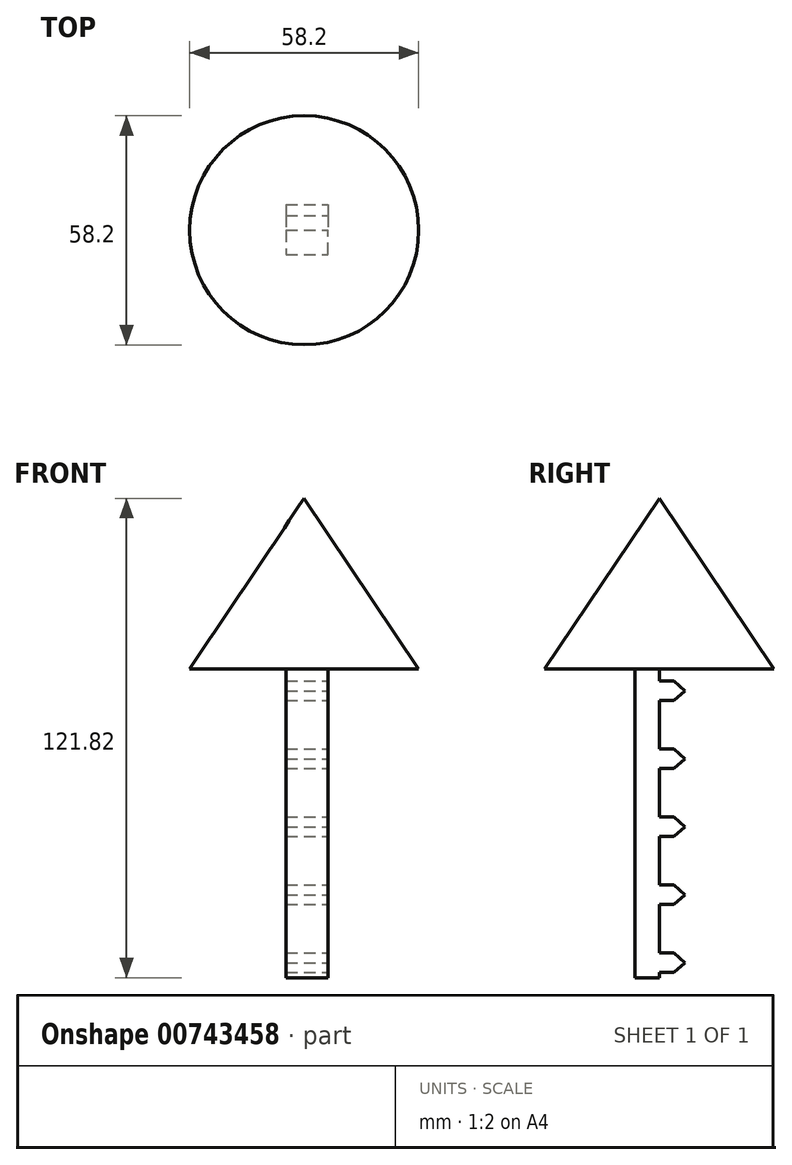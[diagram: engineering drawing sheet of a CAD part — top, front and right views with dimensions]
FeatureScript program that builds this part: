
annotation { "Feature Type Name" : "Feature", "Feature Type Description" : "" }
export const myFeature = defineFeature(function(context is Context, id is Id, definition is map)
    precondition{}
    {
        {
            var Q0;
            Q0=qCreatedBy(makeId("Right.planeOp"),FACE);
            var sketch = newSketch(context, id + "F0", { "sketchPlane" : qUnion([Q0])});
            skLineSegment(sketch, "E0", {"start": v(-29.1, 0) * mm, "end": v(0, 43.33) * mm});
            skLineSegment(sketch, "E1", {"start": v(0, 43.33) * mm, "end": v(0, 0) * mm});
            skLineSegment(sketch, "E2", {"start": v(0, 0) * mm, "end": v(-29.1, 0) * mm});
            skLineSegment(sketch, "E3", {"start": v(61.1, 0) * mm, "end": v(61.1, 40.81) * mm});
            skLineSegment(sketch, "E4.MirrorCS", {"start": v(151.3, 0) * mm, "end": v(122.2, 43.33) * mm});
            skLineSegment(sketch, "E5.MirrorCS", {"start": v(122.2, 43.33) * mm, "end": v(122.2, 0) * mm});
            skLineSegment(sketch, "E6.MirrorCS", {"start": v(122.2, 0) * mm, "end": v(151.3, 0) * mm});
            skSolve(sketch);
        }
        {
            var Q0;
            Q0=makeQuery(id+"F0.imprint","IMPRINT",FACE,{"disambiguationData":[TD([[makeQuery(id+"F0.imprint","IMPRINT",EDGE,{"derivedFrom":sQuery(id+"F0.wireOp",EDGE,"E0")}),-1.0]])]});
            var Q1;
            Q1=sQuery(id+"F0.wireOp",EDGE,"E1");
            revolve(context, id + "F1", {"surfaceOperationType" : NewSurfaceOperationType.NEW, "entities" : qUnion([Q0]), "axis" : qUnion([Q1]), "revolveType" : RevolveType.FULL});
        }
        {
            var Q0;
            Q0=makeQuery(id+"F0.imprint","IMPRINT",FACE,{"disambiguationData":[TD([[makeQuery(id+"F0.imprint","IMPRINT",EDGE,{"derivedFrom":sQuery(id+"F0.wireOp",EDGE,"E4.MirrorCS")}),1.0]])]});
            var Q1;
            Q1=sQuery(id+"F0.wireOp",EDGE,"E5.MirrorCS");
            revolve(context, id + "F2", {"surfaceOperationType" : NewSurfaceOperationType.NEW, "entities" : qUnion([Q0]), "axis" : qUnion([Q1]), "revolveType" : RevolveType.FULL});
        }
        {
            var Q0;
            Q0=makeQuery(id+"F1.opRevolve","SWEPT_FACE",FACE,{"disambiguationData":[OSD([sQuery(id+"F0.wireOp",EDGE,"E2")])]});
            var sketch = newSketch(context, id + "F3", { "sketchPlane" : qUnion([Q0])});
            skLineSegment(sketch, "E7.bottom", {"start": v(-6.7, 6.14) * mm, "end": v(6, 6.14) * mm});
            skLineSegment(sketch, "E7.top", {"start": v(-6.7, -6.56) * mm, "end": v(6, -6.56) * mm});
            skLineSegment(sketch, "E7.left", {"start": v(-6.7, 6.14) * mm, "end": v(-6.7, -6.56) * mm});
            skLineSegment(sketch, "E7.right", {"start": v(6, 6.14) * mm, "end": v(6, -6.56) * mm});
            skSolve(sketch);
        }
        {
            var Q0;
            Q0=makeQuery(id+"F3.imprint","IMPRINT",FACE,{"disambiguationData":[TD([[makeQuery(id+"F3.imprint","IMPRINT",EDGE,{"derivedFrom":sQuery(id+"F3.wireOp",EDGE,"E7.bottom")}),-1.0]])]});
            extrude(context, id + "F4", {"entities" : qUnion([Q0]), "operationType" : NewBodyOperationType.ADD, "depth" : 78.49 * mm, "offsetDistance" : 25.4 * mm});
        }
        {
            var Q0;
            Q0=makeQuery(id+"F4.opExtrude","SWEPT_FACE",FACE,{"disambiguationData":[OSD([sQuery(id+"F3.wireOp",EDGE,"E7.right")])]});
            var sketch = newSketch(context, id + "F5", { "sketchPlane" : qUnion([Q0])});
            skLineSegment(sketch, "E8.0.2.0", {"start": v(0, 52.43) * mm, "end": v(6.56, 52.43) * mm});
            skLineSegment(sketch, "E8.0.2.1", {"start": v(0, 47.52) * mm, "end": v(0, 52.43) * mm});
            skLineSegment(sketch, "E8.0.2.2", {"start": v(6.56, 47.52) * mm, "end": v(0, 47.52) * mm});
            skLineSegment(sketch, "E8.0.3.0", {"start": v(0, 112.37) * mm, "end": v(6.56, 112.37) * mm});
            skLineSegment(sketch, "E8.0.3.1", {"start": v(0, 107.47) * mm, "end": v(0, 112.37) * mm});
            skLineSegment(sketch, "E8.0.3.2", {"start": v(6.56, 107.47) * mm, "end": v(0, 107.47) * mm});
            skLineSegment(sketch, "E8.0.4.0", {"start": v(0, 172.31) * mm, "end": v(6.56, 172.31) * mm});
            skLineSegment(sketch, "E8.0.4.1", {"start": v(0, 167.41) * mm, "end": v(0, 172.31) * mm});
            skLineSegment(sketch, "E8.0.4.2", {"start": v(6.56, 167.41) * mm, "end": v(0, 167.41) * mm});
            skLineSegment(sketch, "E9", {"start": v(0, -3.1) * mm, "end": v(3.77, -3.1) * mm});
            skLineSegment(sketch, "E10", {"start": v(3.77, -3.1) * mm, "end": v(6.56, -5.61) * mm});
            skLineSegment(sketch, "E11", {"start": v(6.56, -5.61) * mm, "end": v(3.77, -7.97) * mm});
            skLineSegment(sketch, "E12", {"start": v(3.77, -7.97) * mm, "end": v(0, -7.97) * mm});
            skLineSegment(sketch, "E13", {"start": v(0, -7.97) * mm, "end": v(0, -3.1) * mm});
            skLineSegment(sketch, "E14.0.1.0", {"start": v(0, -20.38) * mm, "end": v(3.77, -20.38) * mm});
            skLineSegment(sketch, "E14.0.1.1", {"start": v(3.77, -25.24) * mm, "end": v(0, -25.24) * mm});
            skLineSegment(sketch, "E14.0.1.2", {"start": v(0, -25.24) * mm, "end": v(0, -20.38) * mm});
            skLineSegment(sketch, "E14.0.1.3", {"start": v(6.56, -22.88) * mm, "end": v(3.77, -25.24) * mm});
            skLineSegment(sketch, "E14.0.1.4", {"start": v(3.77, -20.38) * mm, "end": v(6.56, -22.88) * mm});
            skLineSegment(sketch, "E14.0.2.0", {"start": v(0, -37.65) * mm, "end": v(3.77, -37.65) * mm});
            skLineSegment(sketch, "E14.0.2.1", {"start": v(3.77, -42.51) * mm, "end": v(0, -42.51) * mm});
            skLineSegment(sketch, "E14.0.2.2", {"start": v(0, -42.51) * mm, "end": v(0, -37.65) * mm});
            skLineSegment(sketch, "E14.0.2.3", {"start": v(6.56, -40.16) * mm, "end": v(3.77, -42.51) * mm});
            skLineSegment(sketch, "E14.0.2.4", {"start": v(3.77, -37.65) * mm, "end": v(6.56, -40.16) * mm});
            skLineSegment(sketch, "E14.0.3.0", {"start": v(0, -54.93) * mm, "end": v(3.77, -54.93) * mm});
            skLineSegment(sketch, "E14.0.3.1", {"start": v(3.77, -59.78) * mm, "end": v(0, -59.78) * mm});
            skLineSegment(sketch, "E14.0.3.2", {"start": v(0, -59.78) * mm, "end": v(0, -54.93) * mm});
            skLineSegment(sketch, "E14.0.3.3", {"start": v(6.56, -57.43) * mm, "end": v(3.77, -59.78) * mm});
            skLineSegment(sketch, "E14.0.3.4", {"start": v(3.77, -54.93) * mm, "end": v(6.56, -57.43) * mm});
            skLineSegment(sketch, "E14.0.4.0", {"start": v(0, -72.2) * mm, "end": v(3.77, -72.2) * mm});
            skLineSegment(sketch, "E14.0.4.1", {"start": v(3.77, -77.05) * mm, "end": v(0, -77.05) * mm});
            skLineSegment(sketch, "E14.0.4.2", {"start": v(0, -77.05) * mm, "end": v(0, -72.2) * mm});
            skLineSegment(sketch, "E14.0.4.3", {"start": v(6.56, -74.7) * mm, "end": v(3.77, -77.05) * mm});
            skLineSegment(sketch, "E14.0.4.4", {"start": v(3.77, -72.2) * mm, "end": v(6.56, -74.7) * mm});
            skLineSegment(sketch, "E14.direction1", {"start": v(0, -7.97) * mm, "end": v(25.4, -7.97) * mm, "construction": true});
            skLineSegment(sketch, "E14.direction2", {"start": v(0, -7.97) * mm, "end": v(0, -25.24) * mm, "construction": true});
            skPoint(sketch, "E15.oppositeSnap0", {"position": v(0, -71.83) * mm});
            skLineSegment(sketch, "E15.bottom", {"start": v(-6.14, 0) * mm, "end": v(0, 0) * mm});
            skLineSegment(sketch, "E15.top", {"start": v(-6.14, -78.49) * mm, "end": v(0, -78.49) * mm});
            skLineSegment(sketch, "E15.left", {"start": v(-6.14, 0) * mm, "end": v(-6.14, -78.49) * mm});
            skLineSegment(sketch, "E15.right", {"start": v(0, 0) * mm, "end": v(0, -78.49) * mm});
            skSolve(sketch);
        }
        {
            var Q0;
            {var subQ15=sQuery(id+"F5.wireOp",EDGE,"E15.bottom");Q0=makeQuery(id+"F5.imprint","IMPRINT",FACE,{"disambiguationData":[TD([[makeQuery(id+"F5.imprint","IMPRINT",EDGE,{"derivedFrom":subQ15}),-1.0]])]});}
            var Q1;
            {var subQ1=sQuery(id+"F5.wireOp",EDGE,"E9");Q1=makeQuery(id+"F5.imprint","IMPRINT",FACE,{"disambiguationData":[TD([[makeQuery(id+"F5.imprint","IMPRINT",EDGE,{"derivedFrom":subQ1}),-1.0]])]});}
            var Q2;
            {var subQ1=sQuery(id+"F5.wireOp",EDGE,"E14.0.1.0");Q2=makeQuery(id+"F5.imprint","IMPRINT",FACE,{"disambiguationData":[TD([[makeQuery(id+"F5.imprint","IMPRINT",EDGE,{"derivedFrom":subQ1}),-1.0]])]});}
            var Q3;
            {var subQ1=sQuery(id+"F5.wireOp",EDGE,"E14.0.2.0");Q3=makeQuery(id+"F5.imprint","IMPRINT",FACE,{"disambiguationData":[TD([[makeQuery(id+"F5.imprint","IMPRINT",EDGE,{"derivedFrom":subQ1}),-1.0]])]});}
            var Q4;
            {var subQ1=sQuery(id+"F5.wireOp",EDGE,"E14.0.3.0");Q4=makeQuery(id+"F5.imprint","IMPRINT",FACE,{"disambiguationData":[TD([[makeQuery(id+"F5.imprint","IMPRINT",EDGE,{"derivedFrom":subQ1}),-1.0]])]});}
            var Q5;
            {var subQ1=sQuery(id+"F5.wireOp",EDGE,"E14.0.4.0");Q5=makeQuery(id+"F5.imprint","IMPRINT",FACE,{"disambiguationData":[TD([[makeQuery(id+"F5.imprint","IMPRINT",EDGE,{"derivedFrom":subQ1}),-1.0]])]});}
            var Q6;
            {var subQ2=sQuery(id+"F5.wireOp",EDGE,"E14.0.5.0");Q6=makeQuery(id+"F5.imprint","IMPRINT",FACE,{"disambiguationData":[TD([[makeQuery(id+"F5.imprint","IMPRINT",EDGE,{"derivedFrom":subQ2}),-1.0]])]});}
            var Q7;
            {var subQ1=sQuery(id+"F5.wireOp",EDGE,"E14.0.6.0");Q7=makeQuery(id+"F5.imprint","IMPRINT",FACE,{"disambiguationData":[TD([[makeQuery(id+"F5.imprint","IMPRINT",EDGE,{"derivedFrom":subQ1}),-1.0]])]});}
            var Q8;
            {var subQ1=sQuery(id+"F5.wireOp",EDGE,"E14.0.7.0");Q8=makeQuery(id+"F5.imprint","IMPRINT",FACE,{"disambiguationData":[TD([[makeQuery(id+"F5.imprint","IMPRINT",EDGE,{"derivedFrom":subQ1}),-1.0]])]});}
            var Q9;
            {var subQ1=sQuery(id+"F5.wireOp",EDGE,"E14.0.8.0");Q9=makeQuery(id+"F5.imprint","IMPRINT",FACE,{"disambiguationData":[TD([[makeQuery(id+"F5.imprint","IMPRINT",EDGE,{"derivedFrom":subQ1}),-1.0]])]});}
            var Q10;
            {var subQ1=sQuery(id+"F5.wireOp",EDGE,"E14.0.9.0");Q10=makeQuery(id+"F5.imprint","IMPRINT",FACE,{"disambiguationData":[TD([[makeQuery(id+"F5.imprint","IMPRINT",EDGE,{"derivedFrom":subQ1}),-1.0]])]});}
            extrude(context, id + "F6", {"entities" : qUnion([Q0, Q1, Q2, Q3, Q4, Q5, Q6, Q7, Q8, Q9, Q10]), "operationType" : NewBodyOperationType.ADD, "oppositeDirection" : true, "depth" : 56.13 * mm, "offsetDistance" : 25.4 * mm});
        }
        {
            var Q0;
            Q0=makeQuery(id+"F2.opRevolve","SWEPT_BODY",BODY,{"disambiguationData":[OSD([sQuery(id+"F0.wireOp",EDGE,"E4.MirrorCS"),sQuery(id+"F0.wireOp",EDGE,"E5.MirrorCS"),sQuery(id+"F0.wireOp",EDGE,"E6.MirrorCS")])]});
            deleteBodies(context, id + "F7", {"entities" : qUnion([Q0])});
        }
        {
            var Q0;
            {var subQ1=sQuery(id+"F5.wireOp",EDGE,"E9");Q0=makeQuery(id+"F5.imprint","IMPRINT",FACE,{"disambiguationData":[TD([[makeQuery(id+"F5.imprint","IMPRINT",EDGE,{"derivedFrom":subQ1}),1.0]])]});}
            var Q1;
            {var subQ3=sQuery(id+"F5.wireOp",EDGE,"E11");Q1=makeQuery(id+"F5.imprint","IMPRINT",FACE,{"disambiguationData":[TD([[makeQuery(id+"F5.imprint","IMPRINT",EDGE,{"derivedFrom":subQ3}),1.0]])]});}
            var Q2;
            {var subQ3=sQuery(id+"F5.wireOp",EDGE,"E14.0.1.1");Q2=makeQuery(id+"F5.imprint","IMPRINT",FACE,{"disambiguationData":[TD([[makeQuery(id+"F5.imprint","IMPRINT",EDGE,{"derivedFrom":subQ3}),1.0]])]});}
            var Q3;
            {var subQ4=sQuery(id+"F5.wireOp",EDGE,"E14.0.2.1");Q3=makeQuery(id+"F5.imprint","IMPRINT",FACE,{"disambiguationData":[TD([[makeQuery(id+"F5.imprint","IMPRINT",EDGE,{"derivedFrom":subQ4}),1.0]])]});}
            var Q4;
            {var subQ4=sQuery(id+"F5.wireOp",EDGE,"E14.0.3.1");Q4=makeQuery(id+"F5.imprint","IMPRINT",FACE,{"disambiguationData":[TD([[makeQuery(id+"F5.imprint","IMPRINT",EDGE,{"derivedFrom":subQ4}),1.0]])]});}
            var Q5;
            {var subQ2=sQuery(id+"F5.wireOp",EDGE,"E14.0.4.1");Q5=makeQuery(id+"F5.imprint","IMPRINT",FACE,{"disambiguationData":[TD([[makeQuery(id+"F5.imprint","IMPRINT",EDGE,{"derivedFrom":subQ2}),1.0]])]});}
            var Q6;
            {var subQ4=sQuery(id+"F5.wireOp",EDGE,"E14.0.5.1");Q6=makeQuery(id+"F5.imprint","IMPRINT",FACE,{"disambiguationData":[TD([[makeQuery(id+"F5.imprint","IMPRINT",EDGE,{"derivedFrom":subQ4}),1.0]])]});}
            var Q7;
            {var subQ3=sQuery(id+"F5.wireOp",EDGE,"E14.0.6.1");Q7=makeQuery(id+"F5.imprint","IMPRINT",FACE,{"disambiguationData":[TD([[makeQuery(id+"F5.imprint","IMPRINT",EDGE,{"derivedFrom":subQ3}),1.0]])]});}
            var Q8;
            {var subQ3=sQuery(id+"F5.wireOp",EDGE,"E14.0.7.1");Q8=makeQuery(id+"F5.imprint","IMPRINT",FACE,{"disambiguationData":[TD([[makeQuery(id+"F5.imprint","IMPRINT",EDGE,{"derivedFrom":subQ3}),1.0]])]});}
            var Q9;
            {var subQ3=sQuery(id+"F5.wireOp",EDGE,"E14.0.8.1");Q9=makeQuery(id+"F5.imprint","IMPRINT",FACE,{"disambiguationData":[TD([[makeQuery(id+"F5.imprint","IMPRINT",EDGE,{"derivedFrom":subQ3}),1.0]])]});}
            var Q10;
            {var subQ6=sQuery(id+"F5.wireOp",EDGE,"E14.0.9.1");Q10=makeQuery(id+"F5.imprint","IMPRINT",FACE,{"disambiguationData":[TD([[makeQuery(id+"F5.imprint","IMPRINT",EDGE,{"derivedFrom":subQ6}),1.0]])]});}
            extrude(context, id + "F8", {"entities" : qUnion([Q0, Q1, Q2, Q3, Q4, Q5, Q6, Q7, Q8, Q9, Q10]), "operationType" : NewBodyOperationType.REMOVE, "oppositeDirection" : true, "depth" : 25.4 * mm, "offsetDistance" : 25.4 * mm});
        }
        {
            var Q0;
            Q0=makeQuery(id+"F6.boolean.opBoolean","MERGE",FACE,{"derivedFrom":[makeQuery(id+"F4.opExtrude","SWEPT_FACE",FACE,{"disambiguationData":[OSD([sQuery(id+"F3.wireOp",EDGE,"E7.bottom")])]}),makeQuery(id+"F6.opExtrude","SWEPT_FACE",FACE,{"disambiguationData":[OSD([sQuery(id+"F5.wireOp",EDGE,"E15.left")])]})]});
            var sketch = newSketch(context, id + "F9", { "sketchPlane" : qUnion([Q0])});
            skLineSegment(sketch, "E16", {"start": v(-4.66, 0) * mm, "end": v(-4.66, -78.49) * mm});
            skSolve(sketch);
        }
        {
            var Q0;
            {var subQ6=sQuery(id+"F9.wireOp",EDGE,"E16");Q0=makeQuery(id+"F9.imprint","IMPRINT",FACE,{"disambiguationData":[TD([[makeQuery(id+"F9.imprint","IMPRINT",EDGE,{"derivedFrom":subQ6}),-1.0]])]});}
            extrude(context, id + "F10", {"entities" : qUnion([Q0]), "operationType" : NewBodyOperationType.REMOVE, "oppositeDirection" : true, "depth" : 25.4 * mm, "offsetDistance" : 25.4 * mm});
        }
    });
